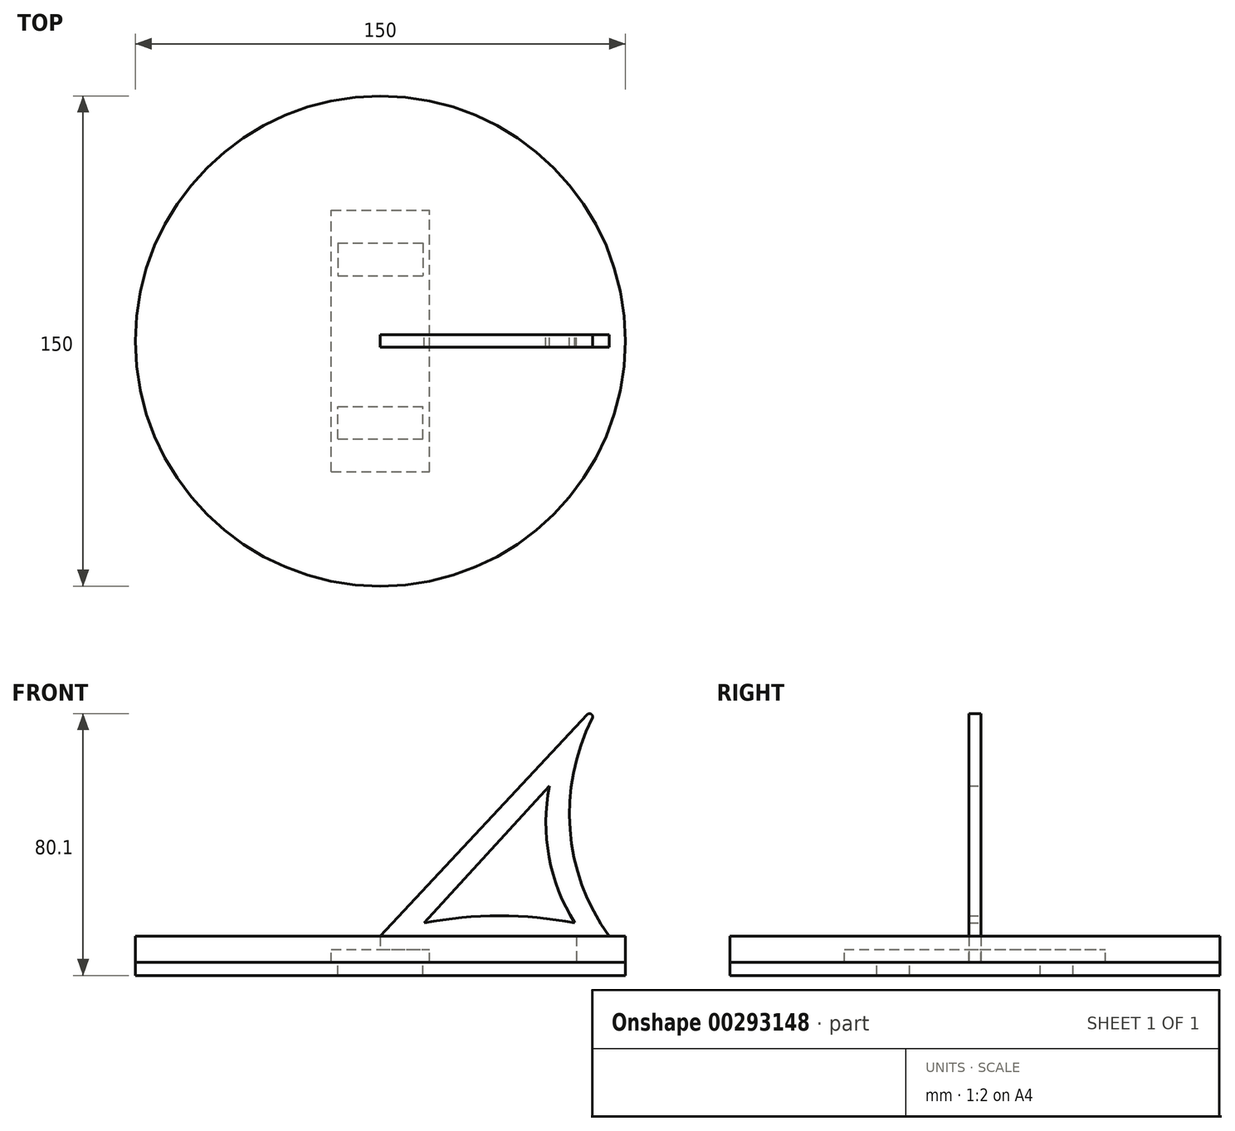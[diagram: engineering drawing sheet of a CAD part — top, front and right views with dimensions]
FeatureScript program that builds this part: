
annotation { "Feature Type Name" : "Feature", "Feature Type Description" : "" }
export const myFeature = defineFeature(function(context is Context, id is Id, definition is map)
    precondition{}
    {
        {
            var Q0;
            Q0=qCreatedBy(makeId("Top.planeOp"),FACE);
            var sketch = newSketch(context, id + "F0", { "sketchPlane" : qUnion([Q0])});
            skCircle(sketch, "E0", {"center": v(0, 0) * mm, "radius": 75 * mm});
            skLineSegment(sketch, "E1.bottom", {"start": v(0, 1.9) * mm, "end": v(60, 1.9) * mm});
            skLineSegment(sketch, "E1.top", {"start": v(0, -1.9) * mm, "end": v(60, -1.9) * mm});
            skLineSegment(sketch, "E1.left", {"start": v(0, 1.9) * mm, "end": v(0, -1.9) * mm});
            skLineSegment(sketch, "E1.right", {"start": v(60, 1.9) * mm, "end": v(60, -1.9) * mm});
            skSolve(sketch);
        }
        {
            var Q0;
            Q0 = qSketchRegion(id + "F0", true);
            extrude(context, id + "F1", {"entities" : qUnion([Q0]), "depth" : 4 * mm});
        }
        {
            var Q0;
            Q0=makeQuery(id+"F1.opExtrude","CAP_FACE",FACE,{"disambiguationData":[OSD([sQuery(id+"F0.wireOp",EDGE,"E0"),sQuery(id+"F0.wireOp",EDGE,"E1.bottom"),sQuery(id+"F0.wireOp",EDGE,"E1.top"),sQuery(id+"F0.wireOp",EDGE,"E1.left"),sQuery(id+"F0.wireOp",EDGE,"E1.right")])],"isStart":true});
            var sketch = newSketch(context, id + "F2", { "sketchPlane" : qUnion([Q0])});
            skCircle(sketch, "E2", {"center": v(0, 0) * mm, "radius": 75 * mm});
            skLineSegment(sketch, "E3.bottom", {"start": v(0, 1.9) * mm, "end": v(60, 1.9) * mm});
            skLineSegment(sketch, "E3.top", {"start": v(0, -1.9) * mm, "end": v(60, -1.9) * mm});
            skLineSegment(sketch, "E3.left", {"start": v(0, 1.9) * mm, "end": v(0, -1.9) * mm});
            skLineSegment(sketch, "E3.right", {"start": v(60, 1.9) * mm, "end": v(60, -1.9) * mm});
            skLineSegment(sketch, "E4.bottom", {"start": v(-15, 40) * mm, "end": v(15, 40) * mm});
            skLineSegment(sketch, "E4.top", {"start": v(-15, -40) * mm, "end": v(15, -40) * mm});
            skLineSegment(sketch, "E4.left", {"start": v(-15, 40) * mm, "end": v(-15, -40) * mm});
            skLineSegment(sketch, "E4.right", {"start": v(15, 40) * mm, "end": v(15, -40) * mm});
            skSolve(sketch);
        }
        {
            var Q0;
            Q0=makeQuery(id+"F2.imprint","IMPRINT",FACE,{"disambiguationData":[TD([[makeQuery(id+"F2.imprint","IMPRINT",EDGE,{"derivedFrom":sQuery(id+"F2.wireOp",EDGE,"E2")}),-1.0]])]});
            extrude(context, id + "F3", {"entities" : qUnion([Q0]), "operationType" : NewBodyOperationType.ADD, "depth" : 4 * mm});
        }
        {
            var Q0;
            Q0=makeQuery(id+"F3.opExtrude","CAP_FACE",FACE,{"disambiguationData":[OSD([sQuery(id+"F2.wireOp",EDGE,"E2"),sQuery(id+"F2.wireOp",EDGE,"E3.bottom"),sQuery(id+"F2.wireOp",EDGE,"E3.top"),sQuery(id+"F2.wireOp",EDGE,"E3.right"),sQuery(id+"F2.wireOp",EDGE,"E4.bottom"),sQuery(id+"F2.wireOp",EDGE,"E4.top"),sQuery(id+"F2.wireOp",EDGE,"E4.left"),sQuery(id+"F2.wireOp",EDGE,"E4.right")])],"isStart":false});
            var sketch = newSketch(context, id + "F4", { "sketchPlane" : qUnion([Q0])});
            skCircle(sketch, "E5", {"center": v(0, 0) * mm, "radius": 75 * mm});
            skLineSegment(sketch, "E6.bottom", {"start": v(-13, 30) * mm, "end": v(13, 30) * mm});
            skLineSegment(sketch, "E6.top", {"start": v(-13, 20) * mm, "end": v(13, 20) * mm});
            skLineSegment(sketch, "E6.left", {"start": v(-13, 30) * mm, "end": v(-13, 20) * mm});
            skLineSegment(sketch, "E6.right", {"start": v(13, 30) * mm, "end": v(13, 20) * mm});
            skLineSegment(sketch, "E7.MirrorCS", {"start": v(13, -30) * mm, "end": v(13, -20) * mm});
            skLineSegment(sketch, "E8.MirrorCS", {"start": v(-13, -30) * mm, "end": v(-13, -20) * mm});
            skLineSegment(sketch, "E9.MirrorCS", {"start": v(-13, -30) * mm, "end": v(13, -30) * mm});
            skLineSegment(sketch, "E10.MirrorCS", {"start": v(-13, -20) * mm, "end": v(13, -20) * mm});
            skSolve(sketch);
        }
        {
            var Q0;
            Q0 = qSketchRegion(id + "F4", true);
            extrude(context, id + "F5", {"entities" : qUnion([Q0]), "depth" : 4 * mm});
        }
        {
            var Q0;
            Q0=makeQuery(id+"F3.boolean.opBoolean","MERGE",FACE,{"derivedFrom":[makeQuery(id+"F1.opExtrude","SWEPT_FACE",FACE,{"disambiguationData":[OSD([sQuery(id+"F0.wireOp",EDGE,"E1.bottom")])]}),makeQuery(id+"F3.opExtrude","SWEPT_FACE",FACE,{"disambiguationData":[OSD([sQuery(id+"F2.wireOp",EDGE,"E3.top")])]})]});
            var sketch = newSketch(context, id + "F6", { "sketchPlane" : qUnion([Q0])});
            skLineSegment(sketch, "E11", {"start": v(0, 0) * mm, "end": v(15, 0) * mm});
            skLineSegment(sketch, "E12", {"start": v(15, 0) * mm, "end": v(15, -4) * mm});
            skLineSegment(sketch, "E13", {"start": v(15, -4) * mm, "end": v(60, -4) * mm});
            skLineSegment(sketch, "E14", {"start": v(60, -4) * mm, "end": v(60, 4) * mm});
            skLineSegment(sketch, "E15", {"start": v(0, 0) * mm, "end": v(0, 4) * mm});
            skLineSegment(sketch, "E16", {"start": v(60, 4) * mm, "end": v(70, 4) * mm});
            skLineSegment(sketch, "E17", {"start": v(0, 4) * mm, "end": v(63.26, 71.78) * mm});
            skArc(sketch, "E18", {"start": v(64.89, 70.65) * mm, "mid": v(58.05, 36.6) * mm, "end": v(70, 4) * mm});
            skArc(sketch, "E19", {"start": v(51.75, 49.93) * mm, "mid": v(51.63, 28.26) * mm, "end": v(59.47, 8.07) * mm});
            skLineSegment(sketch, "E20", {"start": v(51.75, 49.93) * mm, "end": v(13.45, 8.07) * mm});
            skArc(sketch, "E21", {"start": v(59.47, 8.07) * mm, "mid": v(36.46, 10.23) * mm, "end": v(13.45, 8.07) * mm});
            skPoint(sketch, "E22.visualSharp", {"position": v(70, 79) * mm});
            skArc(sketch, "E22.filletArc", {"start": v(64.89, 70.65) * mm, "mid": v(64.57, 71.92) * mm, "end": v(63.26, 71.78) * mm});
            skSolve(sketch);
        }
        {
            var Q0;
            Q0 = qSketchRegion(id + "F6", true);
            extrude(context, id + "F7", {"entities" : qUnion([Q0]), "depth" : 3.8 * mm});
        }
    });
